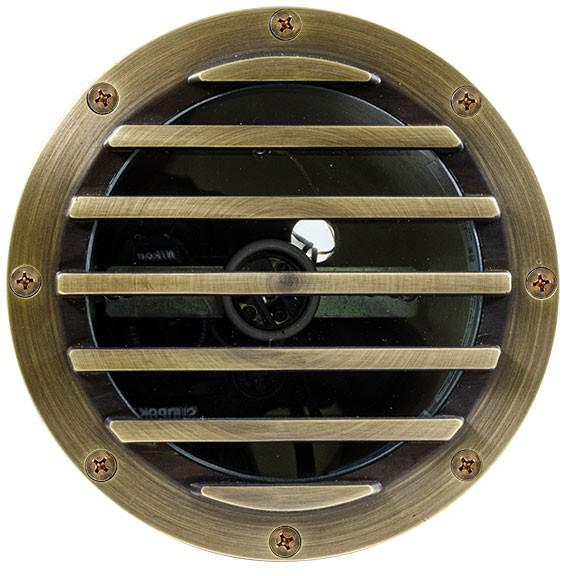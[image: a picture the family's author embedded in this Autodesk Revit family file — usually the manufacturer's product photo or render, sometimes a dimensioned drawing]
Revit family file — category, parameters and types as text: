
# Revit family: Alcon-9031-Revit-Family
name_source: partatom
category: Luminarias
units: mm (PartAtom-declared; Revit-internal decimal feet)

## family parameters
Anfitrión = Cara
Compartido = No
Corte con vacíos al cargar = No
Cota de conector redondo = Usar diámetro
Mantener orientación de anotación = No
Origen de luz = Sí
Punto de cálculo de habitación = No
Tipo de pieza = Normal

## types (1)
- Alcon-9031-Revit-Family
    Cambio de temperatura de color de luz atenuada = <Ninguno>
    Elevación por defecto = 4' - 0"
    Fabricante = Alcon Lighting
    Filtro de color = 16777215
    LENS GLASS = Glass
    Link to IES File = https://www.alconlighting.com
    Longitud de símbolo de origen de luz = 10' - 0"
    Modelo = Alcon Lighting 9031
    Product Data URL = https://www.alconlighting.com
    Product Page = https://www.alconlighting.com
    TOP FINISH = <Por categoría>
    URL = https://www.alconlighting.com
    Ángulo de campo de foco = 90.00°
    Ángulo de enfoque = 30.00°
    Ángulo de inclinación = 60.00°

## geometry (parser evidence)
native form markers: Sweep x2
no freeform markers — native parametric forms only
